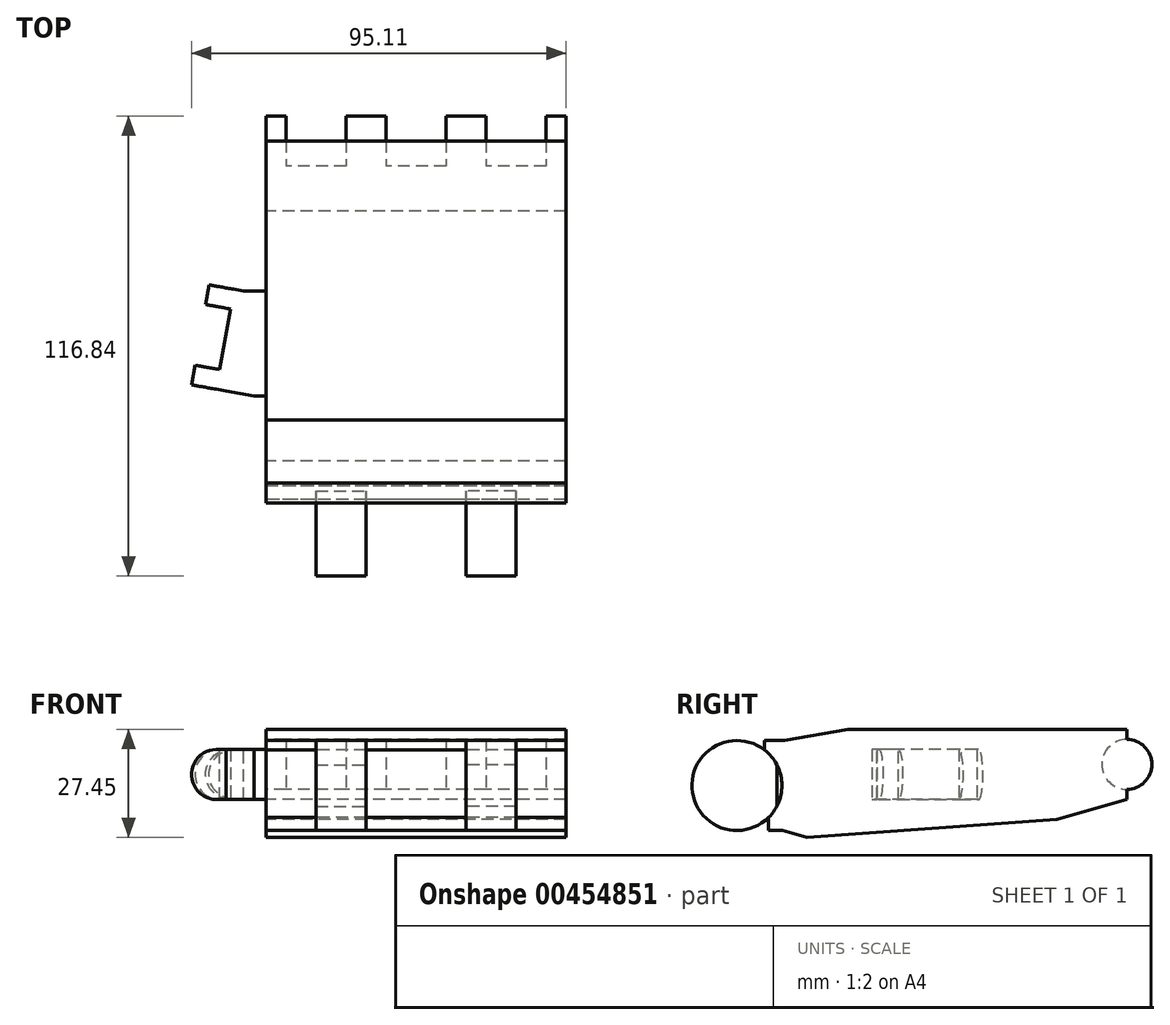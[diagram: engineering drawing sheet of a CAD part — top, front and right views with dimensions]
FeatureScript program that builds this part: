
annotation { "Feature Type Name" : "Feature", "Feature Type Description" : "" }
export const myFeature = defineFeature(function(context is Context, id is Id, definition is map)
    precondition{}
    {
        {
            var Q0;
            Q0=qCreatedBy(makeId("Right.planeOp"),FACE);
            var sketch = newSketch(context, id + "F0", { "sketchPlane" : qUnion([Q0])});
            skLineSegment(sketch, "E0.bottom", {"start": v(44.45, 14) * mm, "end": v(-44.45, 14) * mm});
            skLineSegment(sketch, "E0.left", {"start": v(44.45, 14) * mm, "end": v(44.45, -3.78) * mm});
            skLineSegment(sketch, "E0.right", {"start": v(-44.45, 14) * mm, "end": v(-44.45, -14) * mm});
            skPoint(sketch, "E0.middle", {"position": v(0, 0) * mm});
            skLineSegment(sketch, "E1.bottom", {"start": v(-44.45, 11.17) * mm, "end": v(-47.56, 11.17) * mm});
            skLineSegment(sketch, "E1.top", {"start": v(-44.45, -11.7) * mm, "end": v(-46.56, -11.7) * mm});
            skLineSegment(sketch, "E1.left", {"start": v(-44.45, 11.17) * mm, "end": v(-44.45, -11.7) * mm});
            skLineSegment(sketch, "E1.right", {"start": v(-54.61, 11.17) * mm, "end": v(-54.6, -11.7) * mm});
            skCircle(sketch, "E2", {"center": v(-54.61, -0.26) * mm, "radius": 11.43 * mm});
            skLineSegment(sketch, "E3", {"start": v(44.45, -3.78) * mm, "end": v(26.67, -8.9) * mm});
            skPoint(sketch, "E3.endSnap0", {"position": v(0, -8.9) * mm});
            skLineSegment(sketch, "E4", {"start": v(26.67, -8.9) * mm, "end": v(-44.45, -14) * mm});
            skPoint(sketch, "E0.top.start.orphan", {"position": v(44.45, -14) * mm});
            skLineSegment(sketch, "E5", {"start": v(-46.56, -8.38) * mm, "end": v(-46.56, -11.7) * mm});
            skLineSegment(sketch, "E6", {"start": v(-47.56, 11.17) * mm, "end": v(-47.56, 8.74) * mm});
            skCircle(sketch, "E7", {"center": v(44.45, 5.1) * mm, "radius": 6.35 * mm});
            skSolve(sketch);
        }
        {
            var Q0;
            {var subQ0=sQuery(id+"F0.wireOp",EDGE,"E1.bottom");Q0=makeQuery(id+"F0.imprint","IMPRINT",FACE,{"disambiguationData":[TD([[makeQuery(id+"F0.imprint","IMPRINT",EDGE,{"derivedFrom":subQ0}),1.0]])]});}
            var Q1;
            {var subQ0=sQuery(id+"F0.wireOp",EDGE,"E1.top");Q1=makeQuery(id+"F0.imprint","IMPRINT",FACE,{"disambiguationData":[TD([[makeQuery(id+"F0.imprint","IMPRINT",EDGE,{"derivedFrom":subQ0}),-1.0]])]});}
            var Q2;
            {var subQ4=sQuery(id+"F0.wireOp",EDGE,"E0.bottom");Q2=makeQuery(id+"F0.imprint","IMPRINT",FACE,{"disambiguationData":[TD([[makeQuery(id+"F0.imprint","IMPRINT",EDGE,{"derivedFrom":subQ4}),1.0]])]});}
            extrude(context, id + "F1", {"entities" : qUnion([Q0, Q1, Q2]), "endBound" : BoundingType.SYMMETRIC, "depth" : 76.2 * mm, "offsetDistance" : 25.4 * mm});
        }
        {
            var Q0;
            Q0=makeQuery(id+"F1.opExtrude","SWEPT_EDGE",EDGE,{"disambiguationData":[OSD([sQuery(id+"F0.wireOp",EDGE,"E0.bottom"),sQuery(id+"F0.wireOp",EDGE,"E0.right")])]});
            chamfer(context, id + "F2", {"entities" : qUnion([Q0]), "chamferType" : ChamferType.OFFSET_ANGLE, "width" : 3.17 * mm, "oppositeDirection" : false, "angle" : 80 * degree, "tangentPropagation" : true});
        }
        {
            var Q0;
            Q0=makeQuery(id+"F1.opExtrude","SWEPT_EDGE",EDGE,{"disambiguationData":[OSD([sQuery(id+"F0.wireOp",EDGE,"E0.right"),sQuery(id+"F0.wireOp",EDGE,"E4")])]});
            chamfer(context, id + "F3", {"entities" : qUnion([Q0]), "chamferType" : ChamferType.OFFSET_ANGLE, "width" : 7.62 * mm, "oppositeDirection" : false, "angle" : 20 * degree, "tangentPropagation" : true});
        }
        {
            var Q0;
            {var subQ0=sQuery(id+"F0.wireOp",EDGE,"E2");var subQ1=sQuery(id+"F0.wireOp",EDGE,"E1.left");var subQ2=makeQuery(id+"F0.imprint","INTERSECT",VERTEX,{"disambiguationData":[OD(0.0)],"derivedFrom":[subQ1,subQ0]});Q0=makeQuery(id+"F0.imprint","IMPRINT",FACE,{"disambiguationData":[TD([[makeQuery(id+"F0.imprint","IMPRINT",EDGE,{"disambiguationData":[TD([[subQ2,-1.0]])],"derivedFrom":subQ1}),1.0]])]});}
            var Q1;
            {var subQ1=sQuery(id+"F0.wireOp",EDGE,"E1.right");Q1=makeQuery(id+"F0.imprint","IMPRINT",FACE,{"disambiguationData":[TD([[makeQuery(id+"F0.imprint","IMPRINT",EDGE,{"derivedFrom":subQ1}),1.0]])]});}
            var Q2;
            {var subQ0=sQuery(id+"F0.wireOp",EDGE,"E1.right");Q2=makeQuery(id+"F0.imprint","IMPRINT",FACE,{"disambiguationData":[TD([[makeQuery(id+"F0.imprint","IMPRINT",EDGE,{"derivedFrom":subQ0}),-1.0]])]});}
            extrude(context, id + "F4", {"entities" : qUnion([Q0, Q1, Q2]), "operationType" : NewBodyOperationType.ADD, "depth" : 25.4 * mm, "offsetDistance" : 25.4 * mm, "hasSecondDirection" : true, "secondDirectionOppositeDirection" : false, "secondDirectionDepth" : 12.7 * mm});
        }
        {
            var Q0;
            {var subQ0=sQuery(id+"F0.wireOp",EDGE,"E2");var subQ1=sQuery(id+"F0.wireOp",EDGE,"E1.left");var subQ2=makeQuery(id+"F0.imprint","INTERSECT",VERTEX,{"disambiguationData":[OD(0.0)],"derivedFrom":[subQ1,subQ0]});Q0=makeQuery(id+"F0.imprint","IMPRINT",FACE,{"disambiguationData":[TD([[makeQuery(id+"F0.imprint","IMPRINT",EDGE,{"disambiguationData":[TD([[subQ2,-1.0]])],"derivedFrom":subQ1}),1.0]])]});}
            var Q1;
            {var subQ1=sQuery(id+"F0.wireOp",EDGE,"E1.right");Q1=makeQuery(id+"F0.imprint","IMPRINT",FACE,{"disambiguationData":[TD([[makeQuery(id+"F0.imprint","IMPRINT",EDGE,{"derivedFrom":subQ1}),1.0]])]});}
            var Q2;
            {var subQ0=sQuery(id+"F0.wireOp",EDGE,"E1.right");Q2=makeQuery(id+"F0.imprint","IMPRINT",FACE,{"disambiguationData":[TD([[makeQuery(id+"F0.imprint","IMPRINT",EDGE,{"derivedFrom":subQ0}),-1.0]])]});}
            extrude(context, id + "F5", {"entities" : qUnion([Q0, Q1, Q2]), "operationType" : NewBodyOperationType.ADD, "oppositeDirection" : true, "depth" : 25.4 * mm, "offsetDistance" : 25.4 * mm, "hasSecondDirection" : true, "secondDirectionOppositeDirection" : true, "secondDirectionDepth" : 12.7 * mm});
        }
        {
            var Q0;
            {var subQ0=sQuery(id+"F0.wireOp",EDGE,"E7");var subQ1=sQuery(id+"F0.wireOp",EDGE,"E0.left");var subQ2=makeQuery(id+"F0.imprint","INTERSECT",VERTEX,{"disambiguationData":[OD(0.0)],"derivedFrom":[subQ1,subQ0]});Q0=makeQuery(id+"F0.imprint","IMPRINT",FACE,{"disambiguationData":[TD([[makeQuery(id+"F0.imprint","IMPRINT",EDGE,{"disambiguationData":[TD([[subQ2,-1.0]])],"derivedFrom":subQ1}),1.0]])]});}
            var Q1;
            {var subQ0=sQuery(id+"F0.wireOp",EDGE,"E7");var subQ1=sQuery(id+"F0.wireOp",EDGE,"E0.left");var subQ2=makeQuery(id+"F0.imprint","INTERSECT",VERTEX,{"disambiguationData":[OD(0.0)],"derivedFrom":[subQ1,subQ0]});Q1=makeQuery(id+"F0.imprint","IMPRINT",FACE,{"disambiguationData":[TD([[makeQuery(id+"F0.imprint","IMPRINT",EDGE,{"disambiguationData":[TD([[subQ2,-1.0]])],"derivedFrom":subQ1}),-1.0]])]});}
            extrude(context, id + "F6", {"entities" : qUnion([Q0, Q1]), "operationType" : NewBodyOperationType.ADD, "depth" : 38.1 * mm, "offsetDistance" : 25.4 * mm, "hasSecondDirection" : true, "secondDirectionOppositeDirection" : false, "secondDirectionDepth" : 33.02 * mm});
        }
        {
            var Q0;
            {var subQ0=sQuery(id+"F0.wireOp",EDGE,"E7");var subQ1=sQuery(id+"F0.wireOp",EDGE,"E0.left");var subQ2=makeQuery(id+"F0.imprint","INTERSECT",VERTEX,{"disambiguationData":[OD(0.0)],"derivedFrom":[subQ1,subQ0]});Q0=makeQuery(id+"F0.imprint","IMPRINT",FACE,{"disambiguationData":[TD([[makeQuery(id+"F0.imprint","IMPRINT",EDGE,{"disambiguationData":[TD([[subQ2,-1.0]])],"derivedFrom":subQ1}),1.0]])]});}
            var Q1;
            {var subQ0=sQuery(id+"F0.wireOp",EDGE,"E7");var subQ1=sQuery(id+"F0.wireOp",EDGE,"E0.left");var subQ2=makeQuery(id+"F0.imprint","INTERSECT",VERTEX,{"disambiguationData":[OD(0.0)],"derivedFrom":[subQ1,subQ0]});Q1=makeQuery(id+"F0.imprint","IMPRINT",FACE,{"disambiguationData":[TD([[makeQuery(id+"F0.imprint","IMPRINT",EDGE,{"disambiguationData":[TD([[subQ2,-1.0]])],"derivedFrom":subQ1}),-1.0]])]});}
            extrude(context, id + "F7", {"entities" : qUnion([Q0, Q1]), "operationType" : NewBodyOperationType.ADD, "depth" : 17.78 * mm, "offsetDistance" : 25.4 * mm, "hasSecondDirection" : true, "secondDirectionOppositeDirection" : false, "secondDirectionDepth" : 12.7 * mm});
        }
        {
            var Q0;
            {var subQ0=sQuery(id+"F0.wireOp",EDGE,"E7");var subQ1=sQuery(id+"F0.wireOp",EDGE,"E0.left");var subQ2=makeQuery(id+"F0.imprint","INTERSECT",VERTEX,{"disambiguationData":[OD(0.0)],"derivedFrom":[subQ1,subQ0]});Q0=makeQuery(id+"F0.imprint","IMPRINT",FACE,{"disambiguationData":[TD([[makeQuery(id+"F0.imprint","IMPRINT",EDGE,{"disambiguationData":[TD([[subQ2,-1.0]])],"derivedFrom":subQ1}),1.0]])]});}
            var Q1;
            {var subQ0=sQuery(id+"F0.wireOp",EDGE,"E7");var subQ1=sQuery(id+"F0.wireOp",EDGE,"E0.left");var subQ2=makeQuery(id+"F0.imprint","INTERSECT",VERTEX,{"disambiguationData":[OD(0.0)],"derivedFrom":[subQ1,subQ0]});Q1=makeQuery(id+"F0.imprint","IMPRINT",FACE,{"disambiguationData":[TD([[makeQuery(id+"F0.imprint","IMPRINT",EDGE,{"disambiguationData":[TD([[subQ2,-1.0]])],"derivedFrom":subQ1}),-1.0]])]});}
            extrude(context, id + "F8", {"entities" : qUnion([Q0, Q1]), "operationType" : NewBodyOperationType.ADD, "depth" : 12.7 * mm, "offsetDistance" : 25.4 * mm, "hasSecondDirection" : true, "secondDirectionOppositeDirection" : false, "secondDirectionDepth" : 7.62 * mm});
        }
        {
            var Q0;
            {var subQ0=sQuery(id+"F0.wireOp",EDGE,"E7");var subQ1=sQuery(id+"F0.wireOp",EDGE,"E0.left");var subQ2=makeQuery(id+"F0.imprint","INTERSECT",VERTEX,{"disambiguationData":[OD(0.0)],"derivedFrom":[subQ1,subQ0]});Q0=makeQuery(id+"F0.imprint","IMPRINT",FACE,{"disambiguationData":[TD([[makeQuery(id+"F0.imprint","IMPRINT",EDGE,{"disambiguationData":[TD([[subQ2,-1.0]])],"derivedFrom":subQ1}),1.0]])]});}
            var Q1;
            {var subQ0=sQuery(id+"F0.wireOp",EDGE,"E7");var subQ1=sQuery(id+"F0.wireOp",EDGE,"E0.left");var subQ2=makeQuery(id+"F0.imprint","INTERSECT",VERTEX,{"disambiguationData":[OD(0.0)],"derivedFrom":[subQ1,subQ0]});Q1=makeQuery(id+"F0.imprint","IMPRINT",FACE,{"disambiguationData":[TD([[makeQuery(id+"F0.imprint","IMPRINT",EDGE,{"disambiguationData":[TD([[subQ2,-1.0]])],"derivedFrom":subQ1}),-1.0]])]});}
            extrude(context, id + "F9", {"entities" : qUnion([Q0, Q1]), "operationType" : NewBodyOperationType.ADD, "oppositeDirection" : true, "depth" : 12.7 * mm, "offsetDistance" : 25.4 * mm, "hasSecondDirection" : true, "secondDirectionOppositeDirection" : true, "secondDirectionDepth" : 7.62 * mm});
        }
        {
            var Q0;
            {var subQ0=sQuery(id+"F0.wireOp",EDGE,"E7");var subQ1=sQuery(id+"F0.wireOp",EDGE,"E0.left");var subQ2=makeQuery(id+"F0.imprint","INTERSECT",VERTEX,{"disambiguationData":[OD(0.0)],"derivedFrom":[subQ1,subQ0]});Q0=makeQuery(id+"F0.imprint","IMPRINT",FACE,{"disambiguationData":[TD([[makeQuery(id+"F0.imprint","IMPRINT",EDGE,{"disambiguationData":[TD([[subQ2,-1.0]])],"derivedFrom":subQ1}),1.0]])]});}
            var Q1;
            {var subQ0=sQuery(id+"F0.wireOp",EDGE,"E7");var subQ1=sQuery(id+"F0.wireOp",EDGE,"E0.left");var subQ2=makeQuery(id+"F0.imprint","INTERSECT",VERTEX,{"disambiguationData":[OD(0.0)],"derivedFrom":[subQ1,subQ0]});Q1=makeQuery(id+"F0.imprint","IMPRINT",FACE,{"disambiguationData":[TD([[makeQuery(id+"F0.imprint","IMPRINT",EDGE,{"disambiguationData":[TD([[subQ2,-1.0]])],"derivedFrom":subQ1}),-1.0]])]});}
            extrude(context, id + "F10", {"entities" : qUnion([Q0, Q1]), "operationType" : NewBodyOperationType.ADD, "oppositeDirection" : true, "depth" : 17.78 * mm, "offsetDistance" : 25.4 * mm, "hasSecondDirection" : true, "secondDirectionOppositeDirection" : true, "secondDirectionDepth" : 12.7 * mm});
        }
        {
            var Q0;
            {var subQ0=sQuery(id+"F0.wireOp",EDGE,"E7");var subQ1=sQuery(id+"F0.wireOp",EDGE,"E0.left");var subQ2=makeQuery(id+"F0.imprint","INTERSECT",VERTEX,{"disambiguationData":[OD(0.0)],"derivedFrom":[subQ1,subQ0]});Q0=makeQuery(id+"F0.imprint","IMPRINT",FACE,{"disambiguationData":[TD([[makeQuery(id+"F0.imprint","IMPRINT",EDGE,{"disambiguationData":[TD([[subQ2,-1.0]])],"derivedFrom":subQ1}),-1.0]])]});}
            var Q1;
            {var subQ0=sQuery(id+"F0.wireOp",EDGE,"E7");var subQ1=sQuery(id+"F0.wireOp",EDGE,"E0.left");var subQ2=makeQuery(id+"F0.imprint","INTERSECT",VERTEX,{"disambiguationData":[OD(0.0)],"derivedFrom":[subQ1,subQ0]});Q1=makeQuery(id+"F0.imprint","IMPRINT",FACE,{"disambiguationData":[TD([[makeQuery(id+"F0.imprint","IMPRINT",EDGE,{"disambiguationData":[TD([[subQ2,-1.0]])],"derivedFrom":subQ1}),1.0]])]});}
            extrude(context, id + "F11", {"entities" : qUnion([Q0, Q1]), "operationType" : NewBodyOperationType.ADD, "oppositeDirection" : true, "depth" : 38.1 * mm, "offsetDistance" : 25.4 * mm, "hasSecondDirection" : true, "secondDirectionOppositeDirection" : true, "secondDirectionDepth" : 33.02 * mm});
        }
        {
            var Q0;
            {var subQ0=sQuery(id+"F0.wireOp",EDGE,"E7");Q0=makeQuery(id+"F11.boolean.opBoolean","MERGE",FACE,{"derivedFrom":[makeQuery(id+"F1.opExtrude","CAP_FACE",FACE,{"disambiguationData":[OSD([sQuery(id+"F0.wireOp",EDGE,"E0.bottom"),sQuery(id+"F0.wireOp",EDGE,"E0.left"),sQuery(id+"F0.wireOp",EDGE,"E0.right"),sQuery(id+"F0.wireOp",EDGE,"E1.bottom"),sQuery(id+"F0.wireOp",EDGE,"E1.top"),sQuery(id+"F0.wireOp",EDGE,"E2"),sQuery(id+"F0.wireOp",EDGE,"E3"),sQuery(id+"F0.wireOp",EDGE,"E4"),sQuery(id+"F0.wireOp",EDGE,"E5"),sQuery(id+"F0.wireOp",EDGE,"E6"),subQ0])],"isStart":true}),makeQuery(id+"F11.opExtrude","CAP_FACE",FACE,{"disambiguationData":[OSD([subQ0])],"isStart":false})]});}
            var sketch = newSketch(context, id + "F12", { "sketchPlane" : qUnion([Q0])});
            skLineSegment(sketch, "E8.bottom", {"start": v(-6.35, 8.92) * mm, "end": v(19.05, 8.92) * mm});
            skLineSegment(sketch, "E8.top", {"start": v(-6.35, -3.78) * mm, "end": v(19.05, -3.78) * mm});
            skLineSegment(sketch, "E8.left", {"start": v(-6.35, 8.92) * mm, "end": v(-6.35, -3.78) * mm});
            skLineSegment(sketch, "E8.right", {"start": v(19.05, 8.92) * mm, "end": v(19.05, -3.78) * mm});
            skSolve(sketch);
        }
        {
            var Q0;
            Q0 = qSketchRegion(id + "F12", true);
            extrude(context, id + "F13", {"entities" : qUnion([Q0]), "operationType" : NewBodyOperationType.ADD, "depth" : 10.16 * mm, "offsetDistance" : 25.4 * mm});
        }
        {
            var Q0;
            Q0=makeQuery(id+"F13.opExtrude","CAP_EDGE",EDGE,{"disambiguationData":[OSD([sQuery(id+"F12.wireOp",EDGE,"E8.left")])],"isStart":false});
            chamfer(context, id + "F14", {"entities" : qUnion([Q0]), "chamferType" : ChamferType.OFFSET_ANGLE, "width" : 25.4 * mm, "oppositeDirection" : false, "angle" : 10 * degree, "tangentPropagation" : true});
        }
        {
            var Q0;
            Q0=makeQuery(id+"F14.opChamfer","BLEND_FACE",FACE,{"disambiguationData":[OSD([sQuery(id+"F12.wireOp",EDGE,"E8.left")])]});
            var sketch = newSketch(context, id + "F15", { "sketchPlane" : qUnion([Q0])});
            skLineSegment(sketch, "E9.bottom", {"start": v(1.35, 8.92) * mm, "end": v(27.14, 8.92) * mm});
            skLineSegment(sketch, "E9.top", {"start": v(1.35, -3.78) * mm, "end": v(27.14, -3.78) * mm});
            skLineSegment(sketch, "E9.left", {"start": v(1.35, 8.92) * mm, "end": v(1.35, -3.78) * mm});
            skLineSegment(sketch, "E9.right", {"start": v(27.14, 8.92) * mm, "end": v(27.14, -3.78) * mm});
            skSolve(sketch);
        }
        {
            var Q0;
            Q0 = qSketchRegion(id + "F15", true);
            extrude(context, id + "F16", {"entities" : qUnion([Q0]), "operationType" : NewBodyOperationType.ADD, "depth" : 2.54 * mm, "offsetDistance" : 25.4 * mm});
        }
        {
            var Q0;
            Q0=makeQuery(id+"F16.opExtrude","SWEPT_FACE",FACE,{"disambiguationData":[OSD([sQuery(id+"F15.wireOp",EDGE,"E9.right")])]});
            var sketch = newSketch(context, id + "F17", { "sketchPlane" : qUnion([Q0])});
            skCircle(sketch, "E10", {"center": v(-46.76, 2.57) * mm, "radius": 6.35 * mm});
            skSolve(sketch);
        }
        {
            var Q0;
            Q0 = qSketchRegion(id + "F17", true);
            extrude(context, id + "F18", {"entities" : qUnion([Q0]), "operationType" : NewBodyOperationType.ADD, "oppositeDirection" : true, "depth" : 5.08 * mm, "offsetDistance" : 25.4 * mm});
        }
        {
            var Q0;
            Q0=makeQuery(id+"F16.opExtrude","SWEPT_FACE",FACE,{"disambiguationData":[OSD([sQuery(id+"F15.wireOp",EDGE,"E9.left")])]});
            var sketch = newSketch(context, id + "F19", { "sketchPlane" : qUnion([Q0])});
            skCircle(sketch, "E11", {"center": v(46.76, 2.57) * mm, "radius": 6.35 * mm});
            skSolve(sketch);
        }
        {
            var Q0;
            Q0 = qSketchRegion(id + "F19", true);
            extrude(context, id + "F20", {"entities" : qUnion([Q0]), "operationType" : NewBodyOperationType.ADD, "oppositeDirection" : true, "depth" : 5.08 * mm, "offsetDistance" : 25.4 * mm});
        }
        {
            var Q0;
            Q0=makeQuery(id+"F13.opExtrude","SWEPT_FACE",FACE,{"disambiguationData":[OSD([sQuery(id+"F12.wireOp",EDGE,"E8.right")])]});
            var sketch = newSketch(context, id + "F21", { "sketchPlane" : qUnion([Q0])});
            skLineSegment(sketch, "E12.bottom", {"start": v(-48.26, 8.92) * mm, "end": v(-38.1, 8.92) * mm});
            skLineSegment(sketch, "E12.top", {"start": v(-48.26, -3.78) * mm, "end": v(-38.1, -3.78) * mm});
            skLineSegment(sketch, "E12.left", {"start": v(-48.26, 8.92) * mm, "end": v(-48.26, -3.78) * mm});
            skLineSegment(sketch, "E12.right", {"start": v(-38.1, 8.92) * mm, "end": v(-38.1, -3.78) * mm});
            skSolve(sketch);
        }
        {
            var Q0;
            Q0 = qSketchRegion(id + "F21", true);
            extrude(context, id + "F22", {"entities" : qUnion([Q0]), "operationType" : NewBodyOperationType.ADD, "depth" : 1.27 * mm, "offsetDistance" : 25.4 * mm});
        }
        {
            var Q0;
            Q0=makeQuery(id+"F22.opExtrude","CAP_EDGE",EDGE,{"disambiguationData":[OSD([sQuery(id+"F21.wireOp",EDGE,"E12.left")])],"isStart":false});
            chamfer(context, id + "F23", {"entities" : qUnion([Q0]), "chamferType" : ChamferType.OFFSET_ANGLE, "width" : 7.11 * mm, "oppositeDirection" : false, "angle" : 10 * degree, "tangentPropagation" : true});
        }
    });
